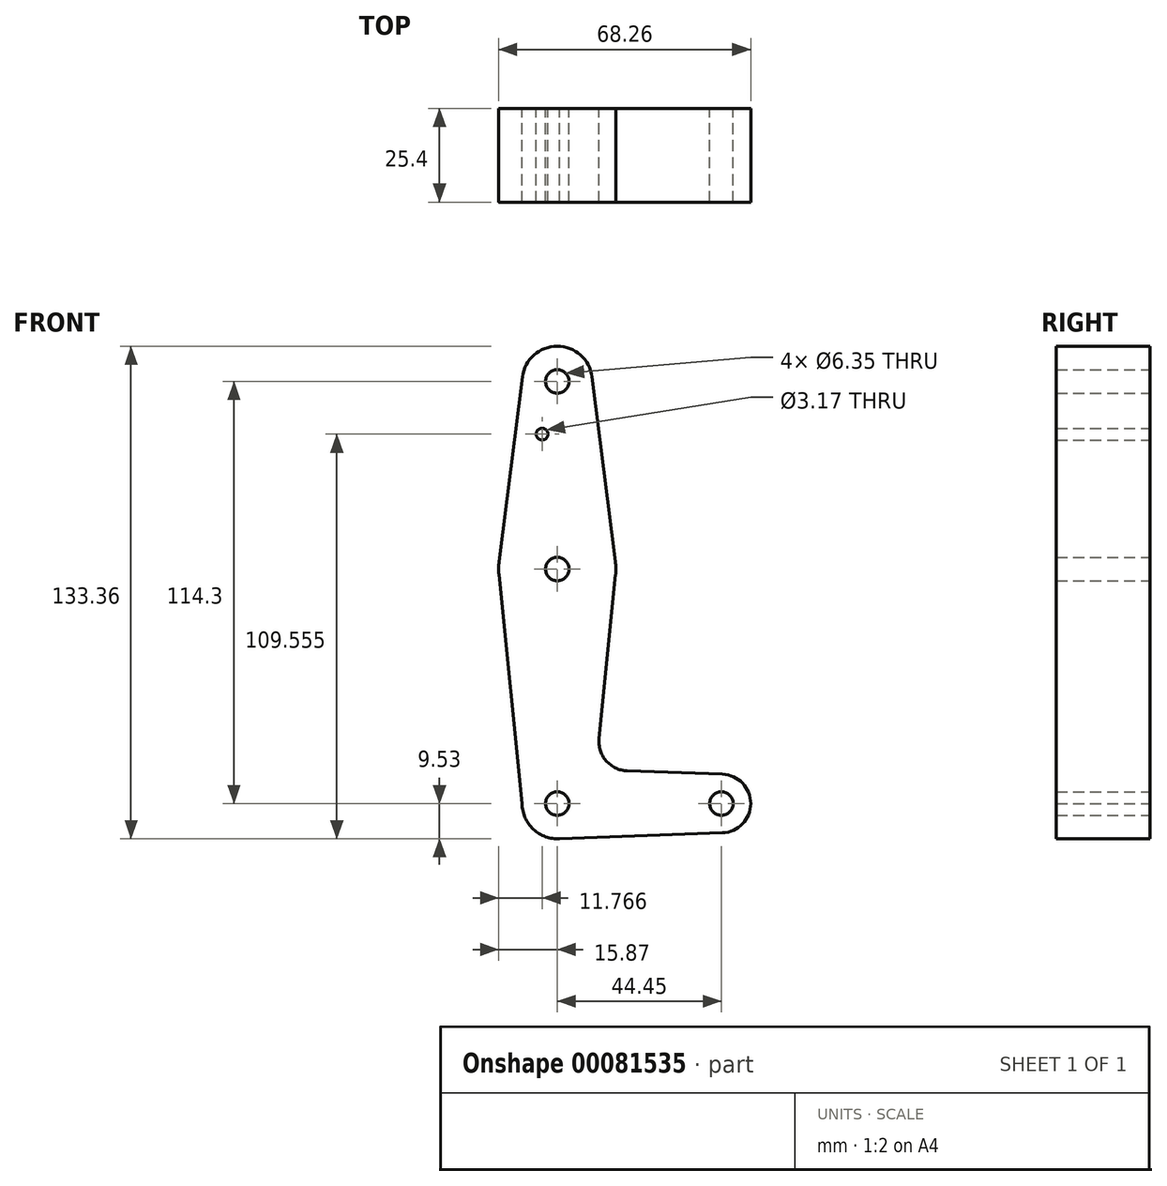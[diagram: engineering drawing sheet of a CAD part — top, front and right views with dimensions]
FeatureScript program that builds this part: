
annotation { "Feature Type Name" : "Feature", "Feature Type Description" : "" }
export const myFeature = defineFeature(function(context is Context, id is Id, definition is map)
    precondition{}
    {
        {
            var Q0;
            Q0=qCreatedBy(makeId("Front.planeOp"),FACE);
            var sketch = newSketch(context, id + "F0", { "sketchPlane" : qUnion([Q0])});
            skLineSegment(sketch, "E0", {"start": v(0, 0) * mm, "end": v(0, 114.3) * mm});
            skLineSegment(sketch, "E1", {"start": v(0, 0) * mm, "end": v(44.45, 0) * mm});
            skCircle(sketch, "E2", {"center": v(0, 114.3) * mm, "radius": 9.53 * mm});
            skCircle(sketch, "E3", {"center": v(0, 0) * mm, "radius": 9.53 * mm});
            skCircle(sketch, "E4", {"center": v(44.45, 0) * mm, "radius": 7.94 * mm});
            skCircle(sketch, "E5", {"center": v(0, 63.5) * mm, "radius": 15.88 * mm});
            skLineSegment(sketch, "E6", {"start": v(9.45, 115.5) * mm, "end": v(15.75, 65.48) * mm});
            skLineSegment(sketch, "E7", {"start": v(-9.45, 115.5) * mm, "end": v(-15.75, 65.48) * mm});
            skLineSegment(sketch, "E8", {"start": v(-9.53, 0) * mm, "end": v(-15.8, 61.9) * mm});
            skCircle(sketch, "E9", {"center": v(0, 0) * mm, "radius": 3.18 * mm});
            skCircle(sketch, "E10", {"center": v(44.45, 0) * mm, "radius": 3.18 * mm});
            skCircle(sketch, "E11", {"center": v(0, 114.3) * mm, "radius": 3.18 * mm});
            skCircle(sketch, "E12", {"center": v(0, 63.5) * mm, "radius": 3.18 * mm});
            skLineSegment(sketch, "E13", {"start": v(11.3, 17.6) * mm, "end": v(15.8, 61.9) * mm});
            skLineSegment(sketch, "E14", {"start": v(18.93, 8.85) * mm, "end": v(44.73, 7.93) * mm});
            skLineSegment(sketch, "E15", {"start": v(0, -9.53) * mm, "end": v(44.73, -7.93) * mm});
            skArc(sketch, "E16.filletArc", {"start": v(11.3, 17.6) * mm, "mid": v(13.22, 11.57) * mm, "end": v(18.93, 8.85) * mm});
            skCircle(sketch, "E17", {"center": v(-4.1, 100.03) * mm, "radius": 1.59 * mm});
            skSolve(sketch);
        }
        {
            var Q0;
            Q0 = qSketchRegion(id + "F0", true);
            var Q1;
            {var subQ0=sQuery(id+"F0.wireOp",EDGE,"E9");var subQ1=sQuery(id+"F0.wireOp",EDGE,"E0");var subQ2=makeQuery(id+"F0.imprint","INTERSECT",VERTEX,{"derivedFrom":[subQ1,subQ0]});Q1=makeQuery(id+"F0.imprint","IMPRINT",FACE,{"disambiguationData":[TD([[makeQuery(id+"F0.imprint","IMPRINT",EDGE,{"disambiguationData":[TD([[subQ2,-1.0]])],"derivedFrom":subQ1}),-1.0]])]});}
            extrude(context, id + "F1", {"entities" : qUnion([Q0, Q1]), "depth" : 25.4 * mm});
        }
    });
